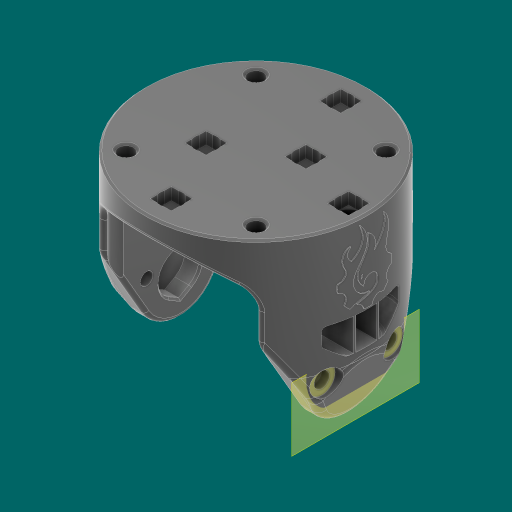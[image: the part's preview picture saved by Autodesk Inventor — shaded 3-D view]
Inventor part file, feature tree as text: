
AUTODESK INVENTOR PART (.ipt)
format: ipt  version: 2023.1 (Build 271208000, 208)  size: 4,691,456 bytes
history: native  units: in
note: dims shown in document units (in); Inventor stores cm internally (conversion verified against a paired STEP export)
features: extrude x17, sketch x15, other x11, chamfer x8, plane x7, fillet x6, projected_geometry x5, mirror x2, split x2, surface_op x1, pattern_circular x1
ambient origin geometry x8: Origin, YZ Plane, XZ Plane, XY Plane, X Axis, Y Axis, Z Axis, Center Point
bodies: Solid1 (feature_tree), Solid2 (feature_tree), Solid3 (feature_tree), Solid4 (feature_tree), Solid5 (feature_tree)
feature tree (75):
  sketch  "Sketch2"  dims[d11=1.2362in d15=2.75in]
  extrude  "Extrusion1"  Depth=2.75in
  plane  "Work Plane1"
  extrude  "Extrusion2"  TaperAngle=45.0deg  [1 undecoded]
  extrude  "Extrusion4"  Depth=1.5748in TaperAngle=360.0deg
  extrude  "Extrusion5"  Depth=0.26in
  fillet  "Fillet2"  Radius=3.0in
  fillet  "Fillet3"  Radius=0.05in
  extrude  "Extrusion11"  Depth=0.05in
  fillet  "Fillet7"  Radius=0.26in
  fillet  "Fillet4"  Radius=0.26in
  fillet  "Fillet5"  Radius=0.26in
  sketch  "Sketch6"  dims[d42=0.26in d43=0.26in d45=3.0in d46=0.05in]
  extrude  "Extrusion6"  Depth=0.7874in TaperAngle=360.0deg
  extrude  "Extrusion7"  Depth=2.75in
  extrude  "Extrusion8"  Depth=0.1in
  plane  "Work Plane4"
  extrude  "Extrusion9"  Depth=0.15in TaperAngle=0.0deg
  extrude  "Extrusion10"  Depth=0.5in
  chamfer  "Chamfer1"  [1 undecoded]
  chamfer  "Chamfer2"  Distance=0.1in
  fillet  "Fillet6"  Radius=0.05in
  chamfer  "Chamfer3"  Distance=3.1437in
  mirror  "Mirror1"
  chamfer  "Chamfer4"  Distance=0.25in
  other  "Ruled Surface1"
  surface_op  "Extend1"
  split  "Split1"
  sketch  "Sketch13"  dims[d65=1.875in d66=0.0in d74=0.0in d75=0.15in d76=0.0in]
  extrude  "Extrusion12"  Depth=0.1in
  plane  "Work Plane5"
  plane  "Work Plane8"
  extrude  "Extrusion13"  Depth=0.1in TaperAngle=0.0deg
  extrude  "Extrusion14"  Depth=0.1in TaperAngle=0.0deg
  chamfer  "Chamfer5"  Distance=0.19in
  split  "Split2"
  pattern_circular  "Circular Pattern1"  Count=4 Angle=360.0deg
  chamfer  "Chamfer6"  Distance=1.0in
  sketch  "Sketch16"  dims[d79=0.25in]
  extrude  "Extrusion15"  Depth=0.1in TaperAngle=0.0deg
  mirror  "Mirror2"
  chamfer  "Chamfer7"  Distance=1.0in
  chamfer  "Chamfer8"  Distance=0.4in
  plane  "Work Plane6"
  extrude  "Extrusion16"  Depth=0.1in
  extrude  "Extrusion17"  Depth=0.1in
  sketch  "Sketch3"  dims[d16=0.8661in d17=45.0deg]
  other  "Work Axis1"
  plane  "Work Plane2"
  sketch  "Sketch5"  dims[d18=0.4724in d35=1.5748in d37=360.0deg]
  sketch  "Sketch7"  dims[d48=0.05in d49=0.05in d50=0.26in d51=0.26in d52=0.26in]
  other  "Work Axis2"
  plane  "Work Plane3"
  sketch  "Sketch8"  dims[d53=0.26in d54=0.7874in d56=360.0deg]
  sketch  "Sketch9"  dims[d58=1.775in d59=0.75in d60=0.0in d61=0.0in d62=2.75in]
  sketch  "Sketch11"  dims[d63=0.1181in d64=0.1in]
  sketch  "3D Sketch2"
  other  "Srf1"
  sketch  "Sketch14"  dims[d77=0.3436in d78=0.5in]
  other  "Srf2"
  sketch  "Sketch17"  dims[d80=30.0deg d81=0.0in d82=0.0in]
  sketch  "Sketch18"  dims[d83=0.375in]
  projected_geometry  "Projected Loop1"
  projected_geometry  "Projected Loop2"
  projected_geometry  "Projected Loop3"
  projected_geometry  "Projected Loop4"
  sketch  "Sketch19"  dims[d84=0.1in d85=0.1in d86=0.05in d87=3.1437in d88=0.25in d89=0.51in d90=0.196in d91=0.0in d92=1.25in d93=0.0in d94=0.19in d95=1.5748in d97=360.0deg d99=1.0in d100=0.0in d101=0.0in d102=0.75in d103=1.0in d104=0.4in d105=0.0in d106=0.26in d107=0.26in d108=0.25in d109=0.0in d110=0.1875in d111=0.125in d112=45.0deg d113=0.1875in d114=0.125in d115=45.0deg d116=0.0472in d117=0.0236in d118=0.125in d119=45.0deg d120=0.275in d121=0.0236in d122=0.125in d123=45.0deg d124=0.196in d125=0.75in d126=0.0in d127=0.0in d128=0.25in d129=1.0in d130=0.0in d131=0.875in d132=0.875in d133=0.19in d134=0.3279in d135=1.0in d136=0.0in d138=1.0in d139=0.0in d140=0.1562in d141=1.0in d142=0.0in d143=0.0236in d144=0.125in d145=45.0deg d146=0.0in d147=0.0in d148=0.7874in d149=360.0deg d151=0.0236in d152=0.125in d153=45.0deg d154=0.0394in d180=0.0118in d181=0.0in d182=0.9in d183=0.698in d192=0.05in d193=0.05in d194=0.0236in d195=0.125in d196=45.0deg d197=0.0236in d198=0.125in d199=45.0deg d200=-0.25in d201=0.33in d202=0.0in d203=0.0in d204=60.0deg d205=0.0276in d206=0.0276in d207=0.196in d208=0.0in d210=0.1in d68=0.0in d69=0.0in d70=0.0in d71=0.0in d209=0.5in d211=0.5in d212=0.0344in]
  projected_geometry  "Projected Loop5"
  other  "<userpath>\Documents\CAD\guardSwerve5\MainAssy.iam"
  other  "MainAssy.iam"
  other  "WheelHalf:1"
  other  "WheelHalf_MIR:1"
  extrude  "ExtrusionSrf1"  Depth=0.1in TaperAngle=0.0deg
  other  "Bevel Gears:1"
  other  "Bevel Gear2:1"
note: 2 required parameter values undecoded (feature->parameter linkage not recoverable at this tier; creation-order binding heuristic only, values carry confidence <= 0.55)
